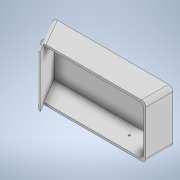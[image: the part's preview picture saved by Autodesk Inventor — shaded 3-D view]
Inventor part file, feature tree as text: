
AUTODESK INVENTOR PART (.ipt)
format: ipt  version: 2021 (Build 250183000, 183)  size: 200,192 bytes
history: native  units: mm
features: sketch x7, extrude x6, fillet x2, chamfer x1, shell x1, hole x1
ambient origin geometry x8: Origin, YZ Plane, XZ Plane, XY Plane, X Axis, Y Axis, Z Axis, Center Point
bodies: Volumenkörper1 (feature_tree)
feature tree (18):
  extrude  "Extrusion1"  Depth=60.0mm
  chamfer  "Fase1"  Distance=40.0mm
  shell  "Wandung1"  Thickness=2.5mm
  extrude  "Extrusion2"  Depth=1.0mm TaperAngle=0.0deg
  hole  "Bohrung1"  [1 undecoded]
  extrude  "Extrusion3"  Depth=10.0mm
  extrude  "Extrusion4"  Depth=10.0mm TaperAngle=0.0deg
  extrude  "Extrusion5"  Depth=6.0mm
  extrude  "Extrusion6"  Depth=6.0mm
  fillet  "Rundung1"  Radius=6.0mm
  fillet  "Rundung2"  Radius=6.0mm
  sketch  "Skizze1"  dims[d0=135.0mm d1=60.0mm d2=40.0mm d3=0.0mm]
  sketch  "Skizze2"  dims[d4=38.0mm d5=2.0mm d6=30.0deg d7=2.5mm]
  sketch  "Skizze3"  dims[d8=9.5mm d9=0.0mm]
  sketch  "Skizze4"  dims[d10=2.0mm d11=6.0mm d12=4.0mm d13=2.0mm d14=90.0deg d15=8.0mm d16=20.594885mm d17=1.0mm d18=0.0mm]
  sketch  "Skizze5"  dims[d19=0.0mm d20=0.0mm d22=2.5mm]
  sketch  "Skizze6"  dims[d23=1.0mm d24=10.0mm]
  sketch  "Skizze7"  dims[d25=22.5mm d26=10.0mm d27=0.0mm d28=6.0mm d29=6.0mm d30=6.0mm d31=6.0mm d32=2.0mm d33=0.0mm d34=4.75mm d35=4.75mm]
note: 1 required parameter value undecoded (feature->parameter linkage not recoverable at this tier; creation-order binding heuristic only, values carry confidence <= 0.55)
